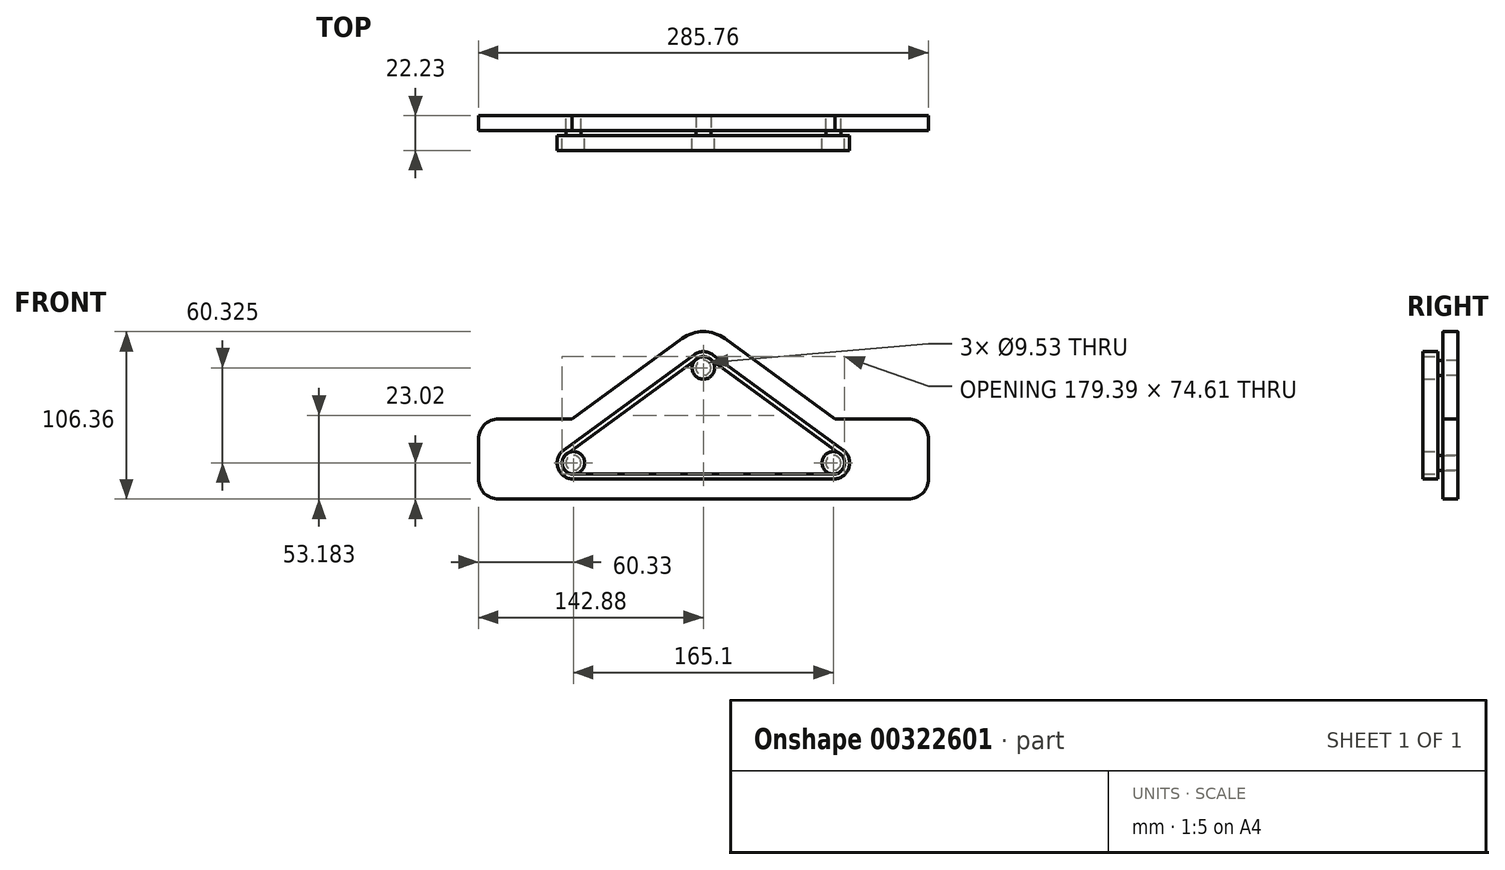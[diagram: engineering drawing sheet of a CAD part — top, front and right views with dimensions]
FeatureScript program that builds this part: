
annotation { "Feature Type Name" : "Feature", "Feature Type Description" : "" }
export const myFeature = defineFeature(function(context is Context, id is Id, definition is map)
    precondition{}
    {
        {
            var Q0;
            Q0=qCreatedBy(makeId("Front.planeOp"),FACE);
            var sketch = newSketch(context, id + "F0", { "sketchPlane" : qUnion([Q0])});
            skCircle(sketch, "E0", {"center": v(-82.55, 0) * mm, "radius": 7.14 * mm});
            skCircle(sketch, "E1", {"center": v(0, 60.33) * mm, "radius": 7.14 * mm});
            skCircle(sketch, "E2", {"center": v(82.55, 0) * mm, "radius": 7.14 * mm});
            skLineSegment(sketch, "E3", {"start": v(-82.55, 0) * mm, "end": v(82.55, 0) * mm, "construction": true});
            skLineSegment(sketch, "E4", {"start": v(0, 60.33) * mm, "end": v(0, 0) * mm, "construction": true});
            skSolve(sketch);
        }
        {
            var Q0;
            Q0=makeQuery(id+"F0.imprint","IMPRINT",FACE,{"disambiguationData":[TD([[makeQuery(id+"F0.imprint","IMPRINT",EDGE,{"derivedFrom":sQuery(id+"F0.wireOp",EDGE,"E1")}),1.0]])]});
            var Q1;
            Q1=makeQuery(id+"F0.imprint","IMPRINT",FACE,{"disambiguationData":[TD([[makeQuery(id+"F0.imprint","IMPRINT",EDGE,{"derivedFrom":sQuery(id+"F0.wireOp",EDGE,"E0")}),1.0]])]});
            var Q2;
            Q2=makeQuery(id+"F0.imprint","IMPRINT",FACE,{"disambiguationData":[TD([[makeQuery(id+"F0.imprint","IMPRINT",EDGE,{"derivedFrom":sQuery(id+"F0.wireOp",EDGE,"E2")}),1.0]])]});
            extrude(context, id + "F1", {"entities" : qUnion([Q0, Q1, Q2]), "depth" : 9.52 * mm});
        }
        {
            var Q0;
            Q0=qCreatedBy(makeId("Front.planeOp"),FACE);
            var sketch = newSketch(context, id + "F2", { "sketchPlane" : qUnion([Q0])});
            skLineSegment(sketch, "E5", {"start": v(-86.76, 5.77) * mm, "end": v(-4.21, 66.1) * mm});
            skLineSegment(sketch, "E6", {"start": v(4.21, 66.1) * mm, "end": v(86.76, 5.77) * mm});
            skLineSegment(sketch, "E7", {"start": v(-82.55, -7.14) * mm, "end": v(82.55, -7.14) * mm});
            skArc(sketch, "E8", {"start": v(-86.76, 5.77) * mm, "mid": v(-89.34, -2.22) * mm, "end": v(-82.55, -7.14) * mm});
            skArc(sketch, "E9", {"start": v(4.21, 66.1) * mm, "mid": v(0, 67.47) * mm, "end": v(-4.21, 66.1) * mm});
            skArc(sketch, "E10", {"start": v(82.55, -7.14) * mm, "mid": v(89.34, -2.22) * mm, "end": v(86.76, 5.77) * mm});
            skArc(sketch, "E11.0", {"start": v(-88.64, 8.33) * mm, "mid": v(-92.36, -3.2) * mm, "end": v(-82.55, -10.32) * mm});
            skArc(sketch, "E11.1", {"start": v(6.09, 68.66) * mm, "mid": v(0, 70.64) * mm, "end": v(-6.09, 68.66) * mm});
            skLineSegment(sketch, "E11.2", {"start": v(6.09, 68.66) * mm, "end": v(88.64, 8.33) * mm});
            skLineSegment(sketch, "E11.3", {"start": v(-88.64, 8.33) * mm, "end": v(-6.09, 68.66) * mm});
            skArc(sketch, "E11.4", {"start": v(82.55, -10.32) * mm, "mid": v(92.36, -3.2) * mm, "end": v(88.64, 8.33) * mm});
            skLineSegment(sketch, "E11.5", {"start": v(-82.55, -10.32) * mm, "end": v(82.55, -10.32) * mm});
            skCircle(sketch, "E12.0", {"center": v(0, 60.33) * mm, "radius": 7.14 * mm, "construction": true});
            skCircle(sketch, "E12.1", {"center": v(-82.55, 0) * mm, "radius": 7.14 * mm, "construction": true});
            skCircle(sketch, "E12.2", {"center": v(82.55, 0) * mm, "radius": 7.14 * mm, "construction": true});
            skSolve(sketch);
        }
        {
            var Q0;
            Q0=makeQuery(id+"F2.imprint","IMPRINT",FACE,{"disambiguationData":[TD([[makeQuery(id+"F2.imprint","IMPRINT",EDGE,{"derivedFrom":sQuery(id+"F2.wireOp",EDGE,"E5")}),1.0]])]});
            var Q1;
            Q1=makeQuery(id+"F1.opExtrude","CAP_FACE",FACE,{"disambiguationData":[OSD([sQuery(id+"F0.wireOp",EDGE,"E1")])],"isStart":false});
            extrude(context, id + "F3", {"entities" : qUnion([Q0]), "endBound" : BoundingType.UP_TO_SURFACE, "endBoundEntityFace" : qUnion([Q1]), "depth" : 25.4 * mm});
        }
        {
            var Q0;
            Q0=makeQuery(id+"F1.opExtrude","CAP_FACE",FACE,{"disambiguationData":[OSD([sQuery(id+"F0.wireOp",EDGE,"E1")])],"isStart":true});
            var sketch = newSketch(context, id + "F4", { "sketchPlane" : qUnion([Q0])});
            skCircle(sketch, "E13", {"center": v(0, 60.33) * mm, "radius": 4.76 * mm});
            skCircle(sketch, "E14", {"center": v(82.55, 0) * mm, "radius": 4.76 * mm});
            skCircle(sketch, "E15", {"center": v(-82.55, 0) * mm, "radius": 4.76 * mm});
            skSolve(sketch);
        }
        {
            var Q0;
            Q0=makeQuery(id+"F4.imprint","IMPRINT",FACE,{"disambiguationData":[TD([[makeQuery(id+"F4.imprint","IMPRINT",EDGE,{"derivedFrom":sQuery(id+"F4.wireOp",EDGE,"E15")}),1.0]])]});
            var Q1;
            Q1=makeQuery(id+"F4.imprint","IMPRINT",FACE,{"disambiguationData":[TD([[makeQuery(id+"F4.imprint","IMPRINT",EDGE,{"derivedFrom":sQuery(id+"F4.wireOp",EDGE,"E14")}),1.0]])]});
            var Q2;
            Q2=makeQuery(id+"F4.imprint","IMPRINT",FACE,{"disambiguationData":[TD([[makeQuery(id+"F4.imprint","IMPRINT",EDGE,{"derivedFrom":sQuery(id+"F4.wireOp",EDGE,"E13")}),1.0]])]});
            extrude(context, id + "F5", {"entities" : qUnion([Q0, Q1, Q2]), "operationType" : NewBodyOperationType.ADD, "depth" : 3.17 * mm + 9.52 * mm});
        }
        {
            var Q0;
            Q0=makeQuery(id+"F5.opExtrude","CAP_FACE",FACE,{"disambiguationData":[OSD([sQuery(id+"F4.wireOp",EDGE,"E13")])],"isStart":false});
            var sketch = newSketch(context, id + "F6", { "sketchPlane" : qUnion([Q0])});
            skLineSegment(sketch, "E16.bottom", {"start": v(-130.18, -23.02) * mm, "end": v(130.18, -23.02) * mm});
            skLineSegment(sketch, "E16.left", {"start": v(-142.88, -10.32) * mm, "end": v(-142.88, 15.08) * mm});
            skLineSegment(sketch, "E16.right", {"start": v(142.88, -10.32) * mm, "end": v(142.88, 15.08) * mm});
            skLineSegment(sketch, "E17", {"start": v(0, 83.34) * mm, "end": v(0, -23.02) * mm, "construction": true});
            skPoint(sketch, "E18", {"position": v(0, 60.33) * mm});
            skCircle(sketch, "E19.0", {"center": v(82.55, 0) * mm, "radius": 4.76 * mm});
            skCircle(sketch, "E20.0", {"center": v(-82.55, 0) * mm, "radius": 4.76 * mm});
            skCircle(sketch, "E21.0", {"center": v(0, 60.33) * mm, "radius": 4.76 * mm});
            skArc(sketch, "E22.1", {"start": v(-13.58, 78.91) * mm, "mid": v(0, 83.34) * mm, "end": v(13.58, 78.91) * mm});
            skLineSegment(sketch, "E22.2", {"start": v(-13.58, 78.91) * mm, "end": v(-83.55, 27.78) * mm});
            skLineSegment(sketch, "E22.3", {"start": v(83.55, 27.78) * mm, "end": v(13.58, 78.91) * mm});
            skLineSegment(sketch, "E22.5", {"start": v(130.18, -23.02) * mm, "end": v(-130.18, -23.02) * mm});
            skLineSegment(sketch, "E23", {"start": v(130.18, 27.78) * mm, "end": v(83.55, 27.78) * mm});
            skLineSegment(sketch, "E24", {"start": v(-130.18, 27.78) * mm, "end": v(-83.55, 27.78) * mm});
            skPoint(sketch, "E25.visualSharp", {"position": v(142.88, 27.78) * mm});
            skArc(sketch, "E25.filletArc", {"start": v(142.88, 15.08) * mm, "mid": v(139.16, 24.06) * mm, "end": v(130.18, 27.78) * mm});
            skPoint(sketch, "E26.visualSharp", {"position": v(142.88, -23.02) * mm});
            skArc(sketch, "E26.filletArc", {"start": v(130.18, -23.02) * mm, "mid": v(139.16, -19.3) * mm, "end": v(142.88, -10.32) * mm});
            skPoint(sketch, "E27.visualSharp", {"position": v(-142.88, -23.02) * mm});
            skArc(sketch, "E27.filletArc", {"start": v(-142.88, -10.32) * mm, "mid": v(-139.16, -19.3) * mm, "end": v(-130.18, -23.02) * mm});
            skPoint(sketch, "E28.visualSharp", {"position": v(-142.88, 27.78) * mm});
            skArc(sketch, "E28.filletArc", {"start": v(-130.18, 27.78) * mm, "mid": v(-139.16, 24.06) * mm, "end": v(-142.88, 15.08) * mm});
            skSolve(sketch);
        }
        {
            var Q0;
            Q0=makeQuery(id+"F6.imprint","IMPRINT",FACE,{"disambiguationData":[TD([[makeQuery(id+"F6.imprint","IMPRINT",EDGE,{"derivedFrom":sQuery(id+"F6.wireOp",EDGE,"E16.bottom")}),1.0]])]});
            var Q1;
            Q1=makeQuery(id+"F6.imprint","IMPRINT",FACE,{"disambiguationData":[TD([[makeQuery(id+"F6.imprint","IMPRINT",EDGE,{"derivedFrom":sQuery(id+"F6.wireOp",EDGE,"E19.0")}),-1.0]])]});
            extrude(context, id + "F7", {"entities" : qUnion([Q0, Q1]), "oppositeDirection" : true, "depth" : 9.52 * mm});
        }
    });
